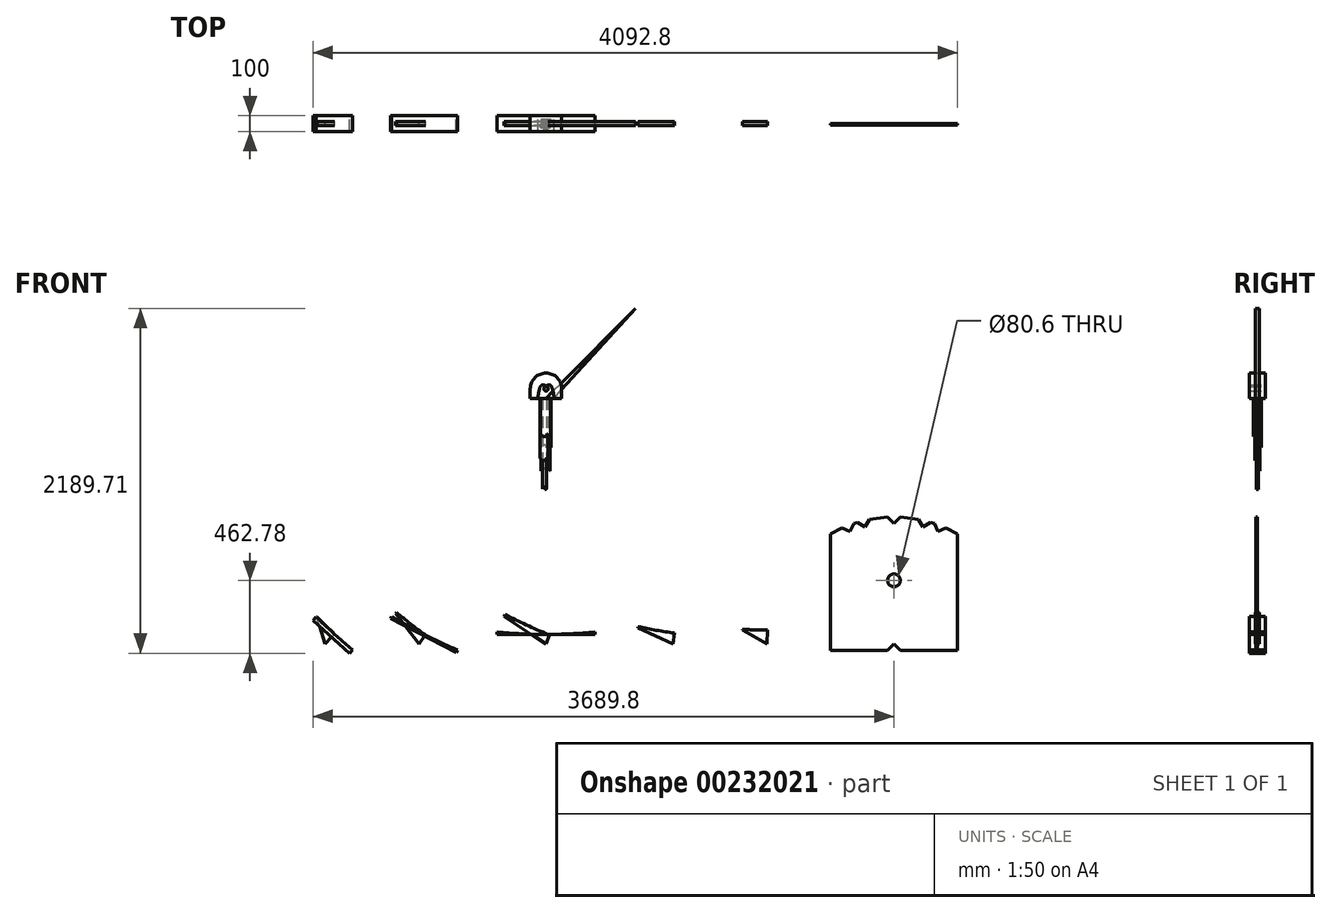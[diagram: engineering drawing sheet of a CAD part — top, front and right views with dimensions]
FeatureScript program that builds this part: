
annotation { "Feature Type Name" : "Feature", "Feature Type Description" : "" }
export const myFeature = defineFeature(function(context is Context, id is Id, definition is map)
    precondition{}
    {
        {
            var Q0;
            Q0=qCreatedBy(makeId("Front.planeOp"),FACE);
            var sketch = newSketch(context, id + "F0", { "sketchPlane" : qUnion([Q0])});
            skCircle(sketch, "E0", {"center": v(0, 0) * mm, "radius": 14 * mm});
            skLineSegment(sketch, "E1", {"start": v(-50, -60) * mm, "end": v(50, -60) * mm, "construction": true});
            skLineSegment(sketch, "E2", {"start": v(0, 0) * mm, "end": v(0, -60) * mm, "construction": true});
            skLineSegment(sketch, "E3", {"start": v(-50, -60) * mm, "end": v(36.5, 12.24) * mm, "construction": true});
            skArc(sketch, "E4", {"start": v(50, -60) * mm, "mid": v(46.6, -23.25) * mm, "end": v(36.5, 12.24) * mm});
            skArc(sketch, "E5", {"start": v(36.5, 12.24) * mm, "mid": v(18.82, 24.99) * mm, "end": v(0, 14) * mm});
            skLineSegment(sketch, "E6", {"start": v(-50, -60) * mm, "end": v(-150, -60) * mm, "construction": true});
            skLineSegment(sketch, "E7.MirrorCS", {"start": v(50, -60) * mm, "end": v(-36.5, 12.24) * mm, "construction": true});
            skArc(sketch, "E8.MirrorCS", {"start": v(-50, -60) * mm, "mid": v(-46.6, -23.25) * mm, "end": v(-36.5, 12.24) * mm});
            skArc(sketch, "E9.MirrorCS", {"start": v(-36.5, 12.24) * mm, "mid": v(-18.82, 24.99) * mm, "end": v(0, 14) * mm});
            skLineSegment(sketch, "E10", {"start": v(0, 120.96) * mm, "end": v(0, -1620) * mm, "construction": true});
            skArc(sketch, "E11", {"start": v(156, -1620) * mm, "mid": v(0, -1464) * mm, "end": v(-156, -1620) * mm, "construction": true});
            skArc(sketch, "E12.1.0.0", {"start": v(-650, -1620) * mm, "mid": v(-806, -1464) * mm, "end": v(-962, -1620) * mm, "construction": true});
            skArc(sketch, "E12.2.0.0", {"start": v(-1248, -1620) * mm, "mid": v(-1404, -1464) * mm, "end": v(-1560, -1620) * mm, "construction": true});
            skLineSegment(sketch, "E13", {"start": v(-806, -1620) * mm, "end": v(0, -1620) * mm, "construction": true});
            skLineSegment(sketch, "E14", {"start": v(-806, -1620) * mm, "end": v(-1404, -1620) * mm, "construction": true});
            skLineSegment(sketch, "E15", {"start": v(-1404, -1620) * mm, "end": v(-2210, -1620) * mm, "construction": true});
            skLineSegment(sketch, "E16", {"start": v(-806, -1620) * mm, "end": v(103.41, 140.15) * mm, "construction": true});
            skLineSegment(sketch, "E17", {"start": v(-1404, -1620) * mm, "end": v(234.43, 200.48) * mm, "construction": true});
            skLineSegment(sketch, "E18.MirrorCS", {"start": v(806, -1620) * mm, "end": v(0, -1620) * mm, "construction": true});
            skArc(sketch, "E19.MirrorCS", {"start": v(650, -1620) * mm, "mid": v(806, -1464) * mm, "end": v(962, -1620) * mm, "construction": true});
            skLineSegment(sketch, "E20.MirrorCS", {"start": v(806, -1620) * mm, "end": v(-103.41, 140.15) * mm, "construction": true});
            skLineSegment(sketch, "E21.MirrorCS", {"start": v(1404, -1620) * mm, "end": v(-234.43, 200.48) * mm, "construction": true});
            skArc(sketch, "E22.MirrorCS", {"start": v(1248, -1620) * mm, "mid": v(1404, -1464) * mm, "end": v(1560, -1620) * mm, "construction": true});
            skLineSegment(sketch, "E23.MirrorCS", {"start": v(1404, -1620) * mm, "end": v(2210, -1620) * mm, "construction": true});
            skLineSegment(sketch, "E24.MirrorCS", {"start": v(806, -1620) * mm, "end": v(1404, -1620) * mm, "construction": true});
            skLineSegment(sketch, "E25", {"start": v(-2210, -1620) * mm, "end": v(-2210, -814) * mm});
            skLineSegment(sketch, "E26", {"start": v(-2210, -1620) * mm, "end": v(-1640.07, -1050.07) * mm, "construction": true});
            skLineSegment(sketch, "E27", {"start": v(-2210, -1620) * mm, "end": v(-1901.56, -875.35) * mm, "construction": true});
            skArc(sketch, "E28", {"start": v(-50, -60) * mm, "mid": v(-47, -77.05) * mm, "end": v(-38.38, -92.05) * mm, "construction": true});
            skLineSegment(sketch, "E29", {"start": v(-38.38, -92.05) * mm, "end": v(0, -60) * mm, "construction": true});
            skArc(sketch, "E30", {"start": v(0, -60) * mm, "mid": v(9.77, -39.12) * mm, "end": v(0, -18.24) * mm, "construction": true});
            skArc(sketch, "E31", {"start": v(-100, 0) * mm, "mid": v(0, 100) * mm, "end": v(100, 0) * mm});
            skLineSegment(sketch, "E32", {"start": v(-100, 0) * mm, "end": v(-100, -60) * mm});
            skLineSegment(sketch, "E33", {"start": v(-100, -60) * mm, "end": v(-50, -60) * mm});
            skLineSegment(sketch, "E34.MirrorCS", {"start": v(100, 0) * mm, "end": v(100, -60) * mm});
            skLineSegment(sketch, "E35.MirrorCS", {"start": v(100, -60) * mm, "end": v(50, -60) * mm});
            skArc(sketch, "E36", {"start": v(-60, -1620) * mm, "mid": v(0, -1560) * mm, "end": v(60, -1620) * mm, "construction": true});
            skArc(sketch, "E37", {"start": v(-874.97, -1620) * mm, "mid": v(-806, -1551.03) * mm, "end": v(-737.03, -1620) * mm, "construction": true});
            skArc(sketch, "E38", {"start": v(-1490.96, -1620) * mm, "mid": v(-1404, -1533.04) * mm, "end": v(-1317.04, -1620) * mm, "construction": true});
            skArc(sketch, "E39.MirrorCS", {"start": v(874.97, -1620) * mm, "mid": v(806, -1551.03) * mm, "end": v(737.03, -1620) * mm, "construction": true});
            skArc(sketch, "E40.MirrorCS", {"start": v(1490.96, -1620) * mm, "mid": v(1404, -1533.04) * mm, "end": v(1317.04, -1620) * mm, "construction": true});
            skArc(sketch, "E41", {"start": v(-1040, -1620) * mm, "mid": v(-806, -1386) * mm, "end": v(-572, -1620) * mm, "construction": true});
            skArc(sketch, "E42", {"start": v(-312, -1620) * mm, "mid": v(0, -1308) * mm, "end": v(312, -1620) * mm, "construction": true});
            skLineSegment(sketch, "E43", {"start": v(-958.6, -1442.61) * mm, "end": v(-1302.26, -1738.26) * mm, "construction": true});
            skLineSegment(sketch, "E44", {"start": v(-211.35, -1390.5) * mm, "end": v(-647.48, -1792.13) * mm, "construction": true});
            skSolve(sketch);
        }
        {
            var Q0;
            Q0=qCreatedBy(makeId("Front.planeOp"),FACE);
            var sketch = newSketch(context, id + "F1", { "sketchPlane" : qUnion([Q0])});
            skPoint(sketch, "E45.0", {"position": v(-1404, -1620) * mm});
            skPoint(sketch, "E46.0", {"position": v(-806, -1620) * mm});
            skPoint(sketch, "E47.0", {"position": v(0, -1620) * mm});
            skPoint(sketch, "E48.0", {"position": v(806, -1620) * mm});
            skPoint(sketch, "E49.0", {"position": v(1404, -1620) * mm});
            skLineSegment(sketch, "E50.0", {"start": v(-1404, -1620) * mm, "end": v(234.43, 200.48) * mm, "construction": true});
            skLineSegment(sketch, "E51.0", {"start": v(-806, -1620) * mm, "end": v(103.41, 140.15) * mm, "construction": true});
            skLineSegment(sketch, "E52.0", {"start": v(0, 120.96) * mm, "end": v(0, -1620) * mm, "construction": true});
            skLineSegment(sketch, "E53.0", {"start": v(806, -1620) * mm, "end": v(-103.41, 140.15) * mm, "construction": true});
            skLineSegment(sketch, "E54.0", {"start": v(1404, -1620) * mm, "end": v(-234.43, 200.48) * mm, "construction": true});
            skLineSegment(sketch, "E55.0", {"start": v(-2210, -1620) * mm, "end": v(-2210, -814) * mm, "construction": true});
            skPoint(sketch, "E56.0", {"position": v(2210, -1620) * mm});
            skArc(sketch, "E57", {"start": v(-1317.04, -1620) * mm, "mid": v(-1404, -1533.04) * mm, "end": v(-1490.96, -1620) * mm, "construction": true});
            skArc(sketch, "E58.1.0.0", {"start": v(-737.03, -1620) * mm, "mid": v(-806, -1551.03) * mm, "end": v(-874.97, -1620) * mm, "construction": true});
            skArc(sketch, "E58.2.0.0", {"start": v(60, -1620) * mm, "mid": v(0, -1560) * mm, "end": v(-60, -1620) * mm, "construction": true});
            skArc(sketch, "E58.3.0.0", {"start": v(874.97, -1620) * mm, "mid": v(806, -1551.03) * mm, "end": v(737.03, -1620) * mm, "construction": true});
            skArc(sketch, "E58.4.0.0", {"start": v(1490.96, -1620) * mm, "mid": v(1404, -1533.04) * mm, "end": v(1317.04, -1620) * mm, "construction": true});
            skLineSegment(sketch, "E59", {"start": v(0, -1620) * mm, "end": v(0, -1560) * mm, "construction": true});
            skLineSegment(sketch, "E60", {"start": v(789.43, -1553.05) * mm, "end": v(806, -1620) * mm, "construction": true});
            skLineSegment(sketch, "E61", {"start": v(1372.32, -1539.02) * mm, "end": v(1404, -1620) * mm, "construction": true});
            skLineSegment(sketch, "E62", {"start": v(-1372.32, -1539.02) * mm, "end": v(-1404, -1620) * mm, "construction": true});
            skLineSegment(sketch, "E63", {"start": v(-789.43, -1553.05) * mm, "end": v(-806, -1620) * mm, "construction": true});
            skLineSegment(sketch, "E64", {"start": v(2210, -1620) * mm, "end": v(2503.62, -869.39) * mm, "construction": true});
            skLineSegment(sketch, "E65", {"start": v(2016.36, -837.6) * mm, "end": v(2210, -1620) * mm, "construction": true});
            skLineSegment(sketch, "E66", {"start": v(2210, -814) * mm, "end": v(2210, -1620) * mm, "construction": true});
            skLineSegment(sketch, "E67", {"start": v(2403.64, -837.6) * mm, "end": v(2210, -1620) * mm, "construction": true});
            skLineSegment(sketch, "E68", {"start": v(1916.38, -869.39) * mm, "end": v(2210, -1620) * mm, "construction": true});
            skLineSegment(sketch, "E69", {"start": v(-1372.32, -1539.02) * mm, "end": v(-825.43, -946.95) * mm, "construction": true});
            skLineSegment(sketch, "E70", {"start": v(-789.43, -1553.05) * mm, "end": v(-413.48, -840.1) * mm, "construction": true});
            skLineSegment(sketch, "E71", {"start": v(0, -1560) * mm, "end": v(0, -754) * mm, "construction": true});
            skLineSegment(sketch, "E72", {"start": v(789.43, -1553.05) * mm, "end": v(413.48, -840.1) * mm, "construction": true});
            skLineSegment(sketch, "E73", {"start": v(1372.32, -1539.02) * mm, "end": v(825.43, -946.95) * mm, "construction": true});
            skLineSegment(sketch, "E74", {"start": v(-1372.32, -1539.02) * mm, "end": v(-1372.32, -733.02) * mm, "construction": true});
            skLineSegment(sketch, "E75", {"start": v(-789.43, -1553.05) * mm, "end": v(-789.43, -747.05) * mm, "construction": true});
            skLineSegment(sketch, "E76", {"start": v(789.43, -1553.05) * mm, "end": v(789.43, -747.05) * mm, "construction": true});
            skLineSegment(sketch, "E77", {"start": v(1372.32, -1539.02) * mm, "end": v(1372.32, -733.02) * mm, "construction": true});
            skCircle(sketch, "E78", {"center": v(2210, -1620) * mm, "radius": 806 * mm, "construction": true});
            skCircle(sketch, "E79", {"center": v(1916.38, -869.39) * mm, "radius": 40.3 * mm, "construction": true});
            skCircle(sketch, "E80", {"center": v(2210, -814) * mm, "radius": 40.3 * mm, "construction": true});
            skCircle(sketch, "E81", {"center": v(2016.36, -837.6) * mm, "radius": 40.3 * mm, "construction": true});
            skCircle(sketch, "E82", {"center": v(2403.64, -837.6) * mm, "radius": 40.3 * mm, "construction": true});
            skCircle(sketch, "E83", {"center": v(2503.62, -869.39) * mm, "radius": 40.3 * mm, "construction": true});
            skLineSegment(sketch, "E84", {"start": v(1879.23, -885) * mm, "end": v(1931.06, -906.92) * mm});
            skLineSegment(sketch, "E85", {"start": v(1931.06, -906.92) * mm, "end": v(1954.27, -855.65) * mm});
            skLineSegment(sketch, "E86", {"start": v(1954.27, -855.65) * mm, "end": v(1977.49, -848.26) * mm});
            skLineSegment(sketch, "E87", {"start": v(1977.49, -848.26) * mm, "end": v(2026.04, -876.73) * mm});
            skLineSegment(sketch, "E88", {"start": v(2026.04, -876.73) * mm, "end": v(2055.7, -828.9) * mm});
            skLineSegment(sketch, "E89", {"start": v(2169.71, -815) * mm, "end": v(2210, -854.3) * mm});
            skLineSegment(sketch, "E90", {"start": v(2210, -854.3) * mm, "end": v(2250.29, -815) * mm});
            skLineSegment(sketch, "E91", {"start": v(2250.29, -815) * mm, "end": v(2364.3, -828.9) * mm});
            skLineSegment(sketch, "E92", {"start": v(2364.3, -828.9) * mm, "end": v(2393.96, -876.73) * mm});
            skLineSegment(sketch, "E93", {"start": v(2393.96, -876.73) * mm, "end": v(2442.51, -848.26) * mm});
            skLineSegment(sketch, "E94", {"start": v(2442.51, -848.26) * mm, "end": v(2465.73, -855.65) * mm});
            skLineSegment(sketch, "E95", {"start": v(2465.73, -855.65) * mm, "end": v(2488.94, -906.92) * mm});
            skLineSegment(sketch, "E96", {"start": v(2488.94, -906.92) * mm, "end": v(2540.77, -885) * mm});
            skLineSegment(sketch, "E97", {"start": v(2055.7, -828.9) * mm, "end": v(2169.71, -815) * mm});
            skLineSegment(sketch, "E98", {"start": v(1807, -1660.3) * mm, "end": v(2169.7, -1660.3) * mm});
            skLineSegment(sketch, "E99", {"start": v(2210, -1620) * mm, "end": v(2210, -1660.3) * mm, "construction": true});
            skArc(sketch, "E100", {"start": v(2250.3, -1660.3) * mm, "mid": v(2210, -1620) * mm, "end": v(2169.7, -1660.3) * mm, "construction": true});
            skLineSegment(sketch, "E101", {"start": v(2210, -1620) * mm, "end": v(3016, -1620) * mm, "construction": true});
            skLineSegment(sketch, "E102", {"start": v(2613, -1660.3) * mm, "end": v(2613, -921.98) * mm});
            skPoint(sketch, "E103", {"position": v(2613, -1620) * mm});
            skLineSegment(sketch, "E104.MirrorCS", {"start": v(1807, -1660.3) * mm, "end": v(1807, -921.98) * mm});
            skLineSegment(sketch, "E105", {"start": v(1879.23, -885) * mm, "end": v(1807, -921.98) * mm});
            skLineSegment(sketch, "E106", {"start": v(2169.7, -1660.3) * mm, "end": v(2210, -1620) * mm});
            skLineSegment(sketch, "E107", {"start": v(2210, -1620) * mm, "end": v(2250.3, -1660.3) * mm});
            skLineSegment(sketch, "E108.trimOffspring", {"start": v(2250.3, -1660.3) * mm, "end": v(2613, -1660.3) * mm});
            skLineSegment(sketch, "E109", {"start": v(2540.77, -885) * mm, "end": v(2613, -921.98) * mm});
            skLineSegment(sketch, "E110", {"start": v(2210, -1620) * mm, "end": v(2210, -814) * mm, "construction": true});
            skCircle(sketch, "E111", {"center": v(2210, -1217) * mm, "radius": 40.3 * mm});
            skSolve(sketch);
        }
        {
            var Q0;
            Q0=qCreatedBy(makeId("Front.planeOp"),FACE);
            var sketch = newSketch(context, id + "F2", { "sketchPlane" : qUnion([Q0])});
            skArc(sketch, "E112.2", {"start": v(60, -1620) * mm, "mid": v(0, -1560) * mm, "end": v(-60, -1620) * mm, "construction": true});
            skLineSegment(sketch, "E113.2", {"start": v(0, 120.96) * mm, "end": v(0, -1620) * mm, "construction": true});
            skLineSegment(sketch, "E114", {"start": v(0, -1620) * mm, "end": v(0, -1560) * mm, "construction": true});
            skLineSegment(sketch, "E115", {"start": v(-312, -1560) * mm, "end": v(312, -1560) * mm, "construction": true});
            skLineSegment(sketch, "E116", {"start": v(-312, -1560) * mm, "end": v(-312, -1545.55) * mm, "construction": true});
            skLineSegment(sketch, "E117", {"start": v(-312, -1545.55) * mm, "end": v(0, 120.96) * mm, "construction": true});
            skLineSegment(sketch, "E118", {"start": v(0, 120.96) * mm, "end": v(312, -1545.55) * mm, "construction": true});
            skLineSegment(sketch, "E119", {"start": v(312, -1545.55) * mm, "end": v(312, -1560) * mm, "construction": true});
            skLineSegment(sketch, "E120", {"start": v(0, -936) * mm, "end": v(0, -1560) * mm, "construction": true});
            skLineSegment(sketch, "E121", {"start": v(0, 120.96) * mm, "end": v(0, -1560) * mm, "construction": true});
            skLineSegment(sketch, "E122", {"start": v(312, -1545.55) * mm, "end": v(312, -921.55) * mm, "construction": true});
            skLineSegment(sketch, "E123", {"start": v(312, -1545.55) * mm, "end": v(0, 1816.43) * mm, "construction": true});
            skArc(sketch, "E124", {"start": v(0, -1560) * mm, "mid": v(-156.17, -1556.39) * mm, "end": v(-312, -1545.55) * mm});
            skLineSegment(sketch, "E125", {"start": v(-312, -1545.55) * mm, "end": v(-312, -921.55) * mm, "construction": true});
            skLineSegment(sketch, "E126", {"start": v(-312, -1545.55) * mm, "end": v(0, 1816.43) * mm, "construction": true});
            skArc(sketch, "E127", {"start": v(0, -1560) * mm, "mid": v(156.17, -1556.39) * mm, "end": v(312, -1545.55) * mm});
            skLineSegment(sketch, "E128", {"start": v(-312, -1545.55) * mm, "end": v(-312, -1560) * mm});
            skLineSegment(sketch, "E129", {"start": v(-312, -1560) * mm, "end": v(312, -1560) * mm});
            skLineSegment(sketch, "E130", {"start": v(312, -1560) * mm, "end": v(312, -1545.55) * mm});
            skLineSegment(sketch, "E131", {"start": v(312, -1545.55) * mm, "end": v(936, -1545.55) * mm, "construction": true});
            skSolve(sketch);
        }
        {
            var Q0;
            Q0=qCreatedBy(makeId("Front.planeOp"),FACE);
            var sketch = newSketch(context, id + "F3", { "sketchPlane" : qUnion([Q0])});
            skArc(sketch, "E132.0", {"start": v(-737.03, -1620) * mm, "mid": v(-806, -1551.03) * mm, "end": v(-874.97, -1620) * mm, "construction": true});
            skLineSegment(sketch, "E133.0", {"start": v(-806, -1620) * mm, "end": v(103.41, 140.15) * mm, "construction": true});
            skLineSegment(sketch, "E134", {"start": v(-806, -1620) * mm, "end": v(-774.51, -1558.64) * mm, "construction": true});
            skLineSegment(sketch, "E135", {"start": v(-982.7, -1451.8) * mm, "end": v(-566.32, -1665.47) * mm, "construction": true});
            skLineSegment(sketch, "E136", {"start": v(-562.05, -1141.65) * mm, "end": v(-774.51, -1558.64) * mm, "construction": true});
            skLineSegment(sketch, "E137", {"start": v(-774.51, -1558.64) * mm, "end": v(103.41, 140.15) * mm, "construction": true});
            skLineSegment(sketch, "E138", {"start": v(-982.7, -1451.8) * mm, "end": v(-979.44, -1445.45) * mm, "construction": true});
            skLineSegment(sketch, "E139", {"start": v(-979.44, -1445.45) * mm, "end": v(103.41, 140.15) * mm, "construction": true});
            skLineSegment(sketch, "E140", {"start": v(-566.32, -1665.47) * mm, "end": v(-563.06, -1659.1) * mm, "construction": true});
            skLineSegment(sketch, "E141", {"start": v(-563.06, -1659.1) * mm, "end": v(103.41, 140.15) * mm, "construction": true});
            skLineSegment(sketch, "E142", {"start": v(-563.06, -1659.1) * mm, "end": v(974.37, 1849.47) * mm, "construction": true});
            skArc(sketch, "E143", {"start": v(-774.51, -1558.64) * mm, "mid": v(-669.55, -1610.5) * mm, "end": v(-563.06, -1659.1) * mm});
            skLineSegment(sketch, "E144", {"start": v(-563.06, -1659.1) * mm, "end": v(-350.6, -1242.12) * mm, "construction": true});
            skArc(sketch, "E145", {"start": v(-774.51, -1558.64) * mm, "mid": v(-877.84, -1503.6) * mm, "end": v(-979.44, -1445.45) * mm});
            skLineSegment(sketch, "E146", {"start": v(975.3, 1851.26) * mm, "end": v(-979.44, -1445.45) * mm, "construction": true});
            skLineSegment(sketch, "E147", {"start": v(-979.44, -1445.45) * mm, "end": v(-766.97, -1028.46) * mm, "construction": true});
            skLineSegment(sketch, "E148", {"start": v(-979.44, -1445.45) * mm, "end": v(-986.8, -1459.79) * mm});
            skLineSegment(sketch, "E149", {"start": v(-986.8, -1459.79) * mm, "end": v(-570.42, -1673.45) * mm});
            skLineSegment(sketch, "E150", {"start": v(-570.42, -1673.45) * mm, "end": v(-563.06, -1659.1) * mm});
            skLineSegment(sketch, "E151", {"start": v(-563.06, -1659.1) * mm, "end": v(-95.06, -1659.1) * mm, "construction": true});
            skSolve(sketch);
        }
        {
            var Q0;
            Q0=qCreatedBy(makeId("Front.planeOp"),FACE);
            var sketch = newSketch(context, id + "F4", { "sketchPlane" : qUnion([Q0])});
            skLineSegment(sketch, "E152.0", {"start": v(-1404, -1620) * mm, "end": v(234.43, 200.48) * mm, "construction": true});
            skArc(sketch, "E153.0", {"start": v(-1317.04, -1620) * mm, "mid": v(-1404, -1533.04) * mm, "end": v(-1490.96, -1620) * mm, "construction": true});
            skLineSegment(sketch, "E154", {"start": v(-1404, -1620) * mm, "end": v(-1345.82, -1555.37) * mm, "construction": true});
            skLineSegment(sketch, "E155", {"start": v(-1345.82, -1555.37) * mm, "end": v(234.43, 200.48) * mm, "construction": true});
            skLineSegment(sketch, "E156", {"start": v(-1345.82, -1555.37) * mm, "end": v(-1137.05, -1323.51) * mm, "construction": true});
            skLineSegment(sketch, "E157", {"start": v(-1461.76, -1451) * mm, "end": v(-1229.88, -1659.74) * mm, "construction": true});
            skLineSegment(sketch, "E158", {"start": v(-1229.88, -1659.74) * mm, "end": v(-1228.16, -1657.83) * mm, "construction": true});
            skLineSegment(sketch, "E159", {"start": v(-1228.16, -1657.83) * mm, "end": v(234.43, 200.48) * mm, "construction": true});
            skLineSegment(sketch, "E160", {"start": v(-1461.76, -1451) * mm, "end": v(-1460.04, -1449.09) * mm, "construction": true});
            skLineSegment(sketch, "E161", {"start": v(-1460.04, -1449.09) * mm, "end": v(234.43, 200.48) * mm, "construction": true});
            skArc(sketch, "E162", {"start": v(-1345.82, -1555.37) * mm, "mid": v(-1287.41, -1607.09) * mm, "end": v(-1228.16, -1657.83) * mm});
            skLineSegment(sketch, "E163", {"start": v(-1228.16, -1657.83) * mm, "end": v(-1019.39, -1425.97) * mm, "construction": true});
            skLineSegment(sketch, "E164", {"start": v(-1228.16, -1657.83) * mm, "end": v(1816.82, 1957.9) * mm, "construction": true});
            skArc(sketch, "E165", {"start": v(-1345.82, -1555.37) * mm, "mid": v(-1403.37, -1502.7) * mm, "end": v(-1460.04, -1449.09) * mm});
            skLineSegment(sketch, "E166", {"start": v(-1251.27, -1217.23) * mm, "end": v(-1460.04, -1449.09) * mm, "construction": true});
            skLineSegment(sketch, "E167", {"start": v(-1460.04, -1449.09) * mm, "end": v(1816.78, 1957.86) * mm, "construction": true});
            skLineSegment(sketch, "E168", {"start": v(-1460.04, -1449.09) * mm, "end": v(-1479.8, -1471.04) * mm});
            skLineSegment(sketch, "E169", {"start": v(-1479.8, -1471.04) * mm, "end": v(-1247.91, -1679.78) * mm});
            skLineSegment(sketch, "E170", {"start": v(-1247.91, -1679.78) * mm, "end": v(-1228.16, -1657.83) * mm});
            skLineSegment(sketch, "E171", {"start": v(-1228.16, -1657.83) * mm, "end": v(-916.16, -1657.83) * mm, "construction": true});
            skSolve(sketch);
        }
        {
            var Q0;
            Q0=qCreatedBy(makeId("Front.planeOp"),FACE);
            var sketch = newSketch(context, id + "F5", { "sketchPlane" : qUnion([Q0])});
            skLineSegment(sketch, "E172.0", {"start": v(-1372.32, -1539.02) * mm, "end": v(-1404, -1620) * mm, "construction": true});
            skLineSegment(sketch, "E173.0", {"start": v(-789.43, -1553.05) * mm, "end": v(-806, -1620) * mm, "construction": true});
            skLineSegment(sketch, "E174.0", {"start": v(789.43, -1553.05) * mm, "end": v(806, -1620) * mm, "construction": true});
            skLineSegment(sketch, "E175.0", {"start": v(0, -1620) * mm, "end": v(0, -1560) * mm, "construction": true});
            skLineSegment(sketch, "E176.0", {"start": v(1372.32, -1539.02) * mm, "end": v(1404, -1620) * mm, "construction": true});
            skLineSegment(sketch, "E177", {"start": v(-1404, -1620) * mm, "end": v(-1690.2, -1508.05) * mm, "construction": true});
            skLineSegment(sketch, "E178", {"start": v(-1690.2, -1508.05) * mm, "end": v(-679.1, -855.58) * mm, "construction": true});
            skLineSegment(sketch, "E179", {"start": v(-679.1, -855.58) * mm, "end": v(-1404, -1620) * mm, "construction": true});
            skLineSegment(sketch, "E180", {"start": v(-806, -1620) * mm, "end": v(-1104.32, -1546.17) * mm, "construction": true});
            skLineSegment(sketch, "E181", {"start": v(-1104.32, -1546.17) * mm, "end": v(-186.52, -767.9) * mm, "construction": true});
            skLineSegment(sketch, "E182", {"start": v(-186.52, -767.9) * mm, "end": v(-806, -1620) * mm, "construction": true});
            skLineSegment(sketch, "E183", {"start": v(-307.32, -1620) * mm, "end": v(396.62, -644.04) * mm, "construction": true});
            skLineSegment(sketch, "E184", {"start": v(396.62, -644.04) * mm, "end": v(0, -1620) * mm, "construction": true});
            skLineSegment(sketch, "E185", {"start": v(806, -1620) * mm, "end": v(507.68, -1693.83) * mm, "construction": true});
            skLineSegment(sketch, "E186", {"start": v(507.68, -1693.83) * mm, "end": v(956.52, -577.33) * mm, "construction": true});
            skLineSegment(sketch, "E187", {"start": v(956.52, -577.33) * mm, "end": v(806, -1620) * mm, "construction": true});
            skLineSegment(sketch, "E188", {"start": v(1404, -1620) * mm, "end": v(1117.8, -1731.95) * mm, "construction": true});
            skLineSegment(sketch, "E189", {"start": v(1117.8, -1731.95) * mm, "end": v(1417.82, -566.61) * mm, "construction": true});
            skLineSegment(sketch, "E190", {"start": v(1417.82, -566.61) * mm, "end": v(1404, -1620) * mm, "construction": true});
            skLineSegment(sketch, "E191.0", {"start": v(0, 120.96) * mm, "end": v(0, -1620) * mm, "construction": true});
            skLineSegment(sketch, "E192.0", {"start": v(-2210, -1620) * mm, "end": v(-1640.07, -1050.07) * mm, "construction": true});
            skArc(sketch, "E193", {"start": v(-1372.32, -1539.02) * mm, "mid": v(-1450.62, -1693.4) * mm, "end": v(-1344.16, -1556.9) * mm});
            skArc(sketch, "E194", {"start": v(-789.43, -1553.05) * mm, "mid": v(-835.1, -1682.52) * mm, "end": v(-765.45, -1564.22) * mm});
            skArc(sketch, "E195", {"start": v(0, -1560) * mm, "mid": v(-11.5, -1678.89) * mm, "end": v(22.59, -1564.41) * mm});
            skArc(sketch, "E196", {"start": v(789.43, -1553.05) * mm, "mid": v(809.42, -1688.88) * mm, "end": v(815.85, -1551.74) * mm});
            skArc(sketch, "E197", {"start": v(1372.32, -1539.02) * mm, "mid": v(1419.56, -1705.55) * mm, "end": v(1405.14, -1533.05) * mm});
            skLineSegment(sketch, "E198", {"start": v(-1457.36, -1449.56) * mm, "end": v(-1230.97, -1664.25) * mm});
            skLineSegment(sketch, "E199", {"start": v(-954.71, -1426.62) * mm, "end": v(-576.18, -1701.82) * mm});
            skLineSegment(sketch, "E200", {"start": v(-266.45, -1446.95) * mm, "end": v(311.63, -1681.88) * mm});
            skLineSegment(sketch, "E201", {"start": v(584.25, -1518.3) * mm, "end": v(1047.45, -1585.18) * mm});
            skLineSegment(sketch, "E202", {"start": v(1249.15, -1531) * mm, "end": v(1561.13, -1535.1) * mm});
            skLineSegment(sketch, "E203", {"start": v(0, 120.96) * mm, "end": v(22.59, -1564.41) * mm, "construction": true});
            skLineSegment(sketch, "E204", {"start": v(22.59, -1564.41) * mm, "end": v(592.52, -994.49) * mm, "construction": true});
            skLineSegment(sketch, "E205", {"start": v(0, -1620) * mm, "end": v(-307.32, -1620) * mm, "construction": true});
            skSolve(sketch);
        }
        {
            var Q0;
            Q0=qCreatedBy(makeId("Front.planeOp"),FACE);
            var sketch = newSketch(context, id + "F6", { "sketchPlane" : qUnion([Q0])});
            skLineSegment(sketch, "E206.0", {"start": v(-266.45, -1446.95) * mm, "end": v(311.63, -1681.88) * mm});
            skLineSegment(sketch, "E207.0", {"start": v(-50, -60) * mm, "end": v(50, -60) * mm, "construction": true});
            skArc(sketch, "E207.1", {"start": v(-50, -60) * mm, "mid": v(-46.6, -23.25) * mm, "end": v(-36.5, 12.24) * mm, "construction": true});
            skArc(sketch, "E207.2", {"start": v(-36.5, 12.24) * mm, "mid": v(-18.82, 24.99) * mm, "end": v(0, 14) * mm, "construction": true});
            skArc(sketch, "E207.3", {"start": v(36.5, 12.24) * mm, "mid": v(18.82, 24.99) * mm, "end": v(0, 14) * mm, "construction": true});
            skArc(sketch, "E207.4", {"start": v(50, -60) * mm, "mid": v(46.6, -23.25) * mm, "end": v(36.5, 12.24) * mm, "construction": true});
            skCircle(sketch, "E207.5", {"center": v(0, 0) * mm, "radius": 14 * mm, "construction": true});
            skLineSegment(sketch, "E208.0", {"start": v(-2210, -1620) * mm, "end": v(-1640.07, -1050.07) * mm, "construction": true});
            skLineSegment(sketch, "E209.0", {"start": v(-312, -1545.55) * mm, "end": v(0, 1816.43) * mm, "construction": true});
            skLineSegment(sketch, "E210.0", {"start": v(312, -1545.55) * mm, "end": v(0, 1816.43) * mm, "construction": true});
            skLineSegment(sketch, "E211", {"start": v(22.59, -1564.41) * mm, "end": v(1293.76, 1563.59) * mm, "construction": true});
            skLineSegment(sketch, "E212", {"start": v(1293.76, 1563.59) * mm, "end": v(-261.02, -1433.57) * mm, "construction": true});
            skLineSegment(sketch, "E213", {"start": v(-261.02, -1433.57) * mm, "end": v(-266.45, -1446.95) * mm, "construction": true});
            skLineSegment(sketch, "E214", {"start": v(-261.02, -1433.57) * mm, "end": v(308.91, -863.64) * mm, "construction": true});
            skLineSegment(sketch, "E215", {"start": v(-261.02, -1433.57) * mm, "end": v(-22.87, -60) * mm, "construction": true});
            skLineSegment(sketch, "E216", {"start": v(1293.76, 1563.59) * mm, "end": v(317.07, -1668.5) * mm, "construction": true});
            skLineSegment(sketch, "E217", {"start": v(317.07, -1668.5) * mm, "end": v(311.63, -1681.88) * mm, "construction": true});
            skLineSegment(sketch, "E218", {"start": v(317.07, -1668.5) * mm, "end": v(887, -1098.57) * mm, "construction": true});
            skLineSegment(sketch, "E219", {"start": v(317.07, -1668.5) * mm, "end": v(-6.44, -60) * mm, "construction": true});
            skLineSegment(sketch, "E220", {"start": v(887, -1098.57) * mm, "end": v(480.5, -692.06) * mm, "construction": true});
            skLineSegment(sketch, "E221", {"start": v(-547.34, -2134.34) * mm, "end": v(22.59, -1564.41) * mm, "construction": true});
            skLineSegment(sketch, "E222", {"start": v(2.43, -60) * mm, "end": v(22.59, -1564.41) * mm, "construction": true});
            skArc(sketch, "E223.0", {"start": v(60, -1620) * mm, "mid": v(0, -1560) * mm, "end": v(-60, -1620) * mm, "construction": true});
            skLineSegment(sketch, "E224.bottom", {"start": v(-22.87, -60) * mm, "end": v(2.43, -60) * mm});
            skLineSegment(sketch, "E224.top", {"start": v(-22.87, -634.89) * mm, "end": v(2.43, -634.89) * mm, "construction": true});
            skLineSegment(sketch, "E224.left", {"start": v(2.43, -60) * mm, "end": v(2.43, -634.89) * mm});
            skLineSegment(sketch, "E224.right", {"start": v(-22.87, -60) * mm, "end": v(-22.87, -634.89) * mm});
            skLineSegment(sketch, "E225.bottom", {"start": v(-6.44, -60) * mm, "end": v(2.43, -60) * mm});
            skLineSegment(sketch, "E225.top", {"start": v(-6.44, -634.89) * mm, "end": v(2.43, -634.89) * mm, "construction": true});
            skLineSegment(sketch, "E225.right", {"start": v(-6.44, -60) * mm, "end": v(-6.44, -634.89) * mm});
            skArc(sketch, "E226", {"start": v(2.43, -634.89) * mm, "mid": v(-2, -639.32) * mm, "end": v(-6.44, -634.89) * mm});
            skArc(sketch, "E227", {"start": v(-22.87, -634.89) * mm, "mid": v(-10.22, -622.24) * mm, "end": v(2.43, -634.89) * mm});
            skSolve(sketch);
        }
        {
            var Q0;
            Q0=qCreatedBy(makeId("Front.planeOp"),FACE);
            var sketch = newSketch(context, id + "F7", { "sketchPlane" : qUnion([Q0])});
            skLineSegment(sketch, "E228.0", {"start": v(-50, -60) * mm, "end": v(50, -60) * mm, "construction": true});
            skArc(sketch, "E229.0", {"start": v(-50, -60) * mm, "mid": v(-46.6, -23.25) * mm, "end": v(-36.5, 12.24) * mm, "construction": true});
            skArc(sketch, "E229.1", {"start": v(-36.5, 12.24) * mm, "mid": v(-18.82, 24.99) * mm, "end": v(0, 14) * mm, "construction": true});
            skCircle(sketch, "E229.2", {"center": v(0, 0) * mm, "radius": 14 * mm, "construction": true});
            skArc(sketch, "E229.3", {"start": v(36.5, 12.24) * mm, "mid": v(18.82, 24.99) * mm, "end": v(0, 14) * mm, "construction": true});
            skArc(sketch, "E229.4", {"start": v(50, -60) * mm, "mid": v(46.6, -23.25) * mm, "end": v(36.5, 12.24) * mm, "construction": true});
            skLineSegment(sketch, "E230.0", {"start": v(-954.71, -1426.62) * mm, "end": v(-576.18, -1701.82) * mm});
            skLineSegment(sketch, "E231.0", {"start": v(584.25, -1518.3) * mm, "end": v(1047.45, -1585.18) * mm});
            skPoint(sketch, "E232.0", {"position": v(-765.45, -1564.22) * mm});
            skPoint(sketch, "E233.0", {"position": v(815.85, -1551.74) * mm});
            skLineSegment(sketch, "E234.0", {"start": v(975.3, 1851.26) * mm, "end": v(-979.44, -1445.45) * mm, "construction": true});
            skLineSegment(sketch, "E234.1", {"start": v(-563.06, -1659.1) * mm, "end": v(974.37, 1849.47) * mm, "construction": true});
            skLineSegment(sketch, "E235", {"start": v(815.85, -1551.74) * mm, "end": v(1363.17, 2239.6) * mm, "construction": true});
            skLineSegment(sketch, "E236", {"start": v(1363.17, 2239.6) * mm, "end": v(585.28, -1511.23) * mm, "construction": true});
            skLineSegment(sketch, "E237", {"start": v(585.28, -1511.23) * mm, "end": v(584.25, -1518.3) * mm, "construction": true});
            skLineSegment(sketch, "E238", {"start": v(585.28, -1511.23) * mm, "end": v(1155.2, -941.3) * mm, "construction": true});
            skLineSegment(sketch, "E239", {"start": v(585.28, -1511.23) * mm, "end": v(11.67, -60) * mm, "construction": true});
            skLineSegment(sketch, "E240.0", {"start": v(-2210, -1620) * mm, "end": v(-1640.07, -1050.07) * mm, "construction": true});
            skLineSegment(sketch, "E241", {"start": v(478.55, -2148.03) * mm, "end": v(1048.47, -1578.1) * mm, "construction": true});
            skLineSegment(sketch, "E242", {"start": v(-37.24, -60) * mm, "end": v(1048.47, -1578.1) * mm, "construction": true});
            skLineSegment(sketch, "E243", {"start": v(1047.45, -1585.18) * mm, "end": v(1048.47, -1578.1) * mm, "construction": true});
            skLineSegment(sketch, "E244", {"start": v(815.85, -1551.74) * mm, "end": v(1363.46, 2241.6) * mm, "construction": true});
            skLineSegment(sketch, "E245", {"start": v(1363.46, 2241.6) * mm, "end": v(1048.47, -1578.1) * mm, "construction": true});
            skLineSegment(sketch, "E246", {"start": v(478.55, -2148.03) * mm, "end": v(213.51, -1883) * mm, "construction": true});
            skLineSegment(sketch, "E247", {"start": v(-1520.44, -1990.76) * mm, "end": v(-950.5, -1420.84) * mm, "construction": true});
            skLineSegment(sketch, "E248", {"start": v(-31.38, -60) * mm, "end": v(-950.5, -1420.84) * mm, "construction": true});
            skLineSegment(sketch, "E249", {"start": v(-765.45, -1564.22) * mm, "end": v(1488.29, 1535.78) * mm, "construction": true});
            skLineSegment(sketch, "E250", {"start": v(1488.29, 1535.78) * mm, "end": v(-950.5, -1420.84) * mm, "construction": true});
            skLineSegment(sketch, "E251", {"start": v(-950.5, -1420.84) * mm, "end": v(-954.71, -1426.62) * mm, "construction": true});
            skLineSegment(sketch, "E252", {"start": v(-576.18, -1701.82) * mm, "end": v(-571.97, -1696.03) * mm, "construction": true});
            skLineSegment(sketch, "E253", {"start": v(-765.45, -1564.22) * mm, "end": v(1487.1, 1534.14) * mm, "construction": true});
            skLineSegment(sketch, "E254", {"start": v(1487.1, 1534.14) * mm, "end": v(-571.97, -1696.03) * mm, "construction": true});
            skLineSegment(sketch, "E255", {"start": v(-1468.77, -1939.1) * mm, "end": v(-1141.9, -2265.96) * mm, "construction": true});
            skLineSegment(sketch, "E256", {"start": v(-571.97, -1696.03) * mm, "end": v(-1141.9, -2265.96) * mm, "construction": true});
            skLineSegment(sketch, "E257", {"start": v(24.5, -60) * mm, "end": v(-571.97, -1696.03) * mm, "construction": true});
            skLineSegment(sketch, "E258", {"start": v(1385.78, -981.81) * mm, "end": v(815.85, -1551.74) * mm, "construction": true});
            skLineSegment(sketch, "E259", {"start": v(815.85, -1551.74) * mm, "end": v(3.51, -60) * mm, "construction": true});
            skLineSegment(sketch, "E260", {"start": v(-1335.37, -2134.15) * mm, "end": v(-765.45, -1564.22) * mm, "construction": true});
            skLineSegment(sketch, "E261", {"start": v(2.16, -60) * mm, "end": v(-765.45, -1564.22) * mm, "construction": true});
            skArc(sketch, "E262.0", {"start": v(-737.03, -1620) * mm, "mid": v(-806, -1551.03) * mm, "end": v(-874.97, -1620) * mm, "construction": true});
            skArc(sketch, "E263.0", {"start": v(874.97, -1620) * mm, "mid": v(806, -1551.03) * mm, "end": v(737.03, -1620) * mm, "construction": true});
            skLineSegment(sketch, "E264.bottom", {"start": v(3.51, -60) * mm, "end": v(11.67, -60) * mm});
            skLineSegment(sketch, "E264.top", {"start": v(3.51, -434.82) * mm, "end": v(11.67, -434.82) * mm, "construction": true});
            skLineSegment(sketch, "E264.left", {"start": v(11.67, -60) * mm, "end": v(11.67, -434.82) * mm});
            skLineSegment(sketch, "E264.right", {"start": v(3.51, -60) * mm, "end": v(3.51, -434.82) * mm});
            skArc(sketch, "E265", {"start": v(11.67, -434.82) * mm, "mid": v(7.6, -438.9) * mm, "end": v(3.51, -434.82) * mm});
            skLineSegment(sketch, "E266.bottom", {"start": v(-37.24, -60) * mm, "end": v(3.51, -60) * mm});
            skLineSegment(sketch, "E266.top", {"start": v(-37.24, -434.82) * mm, "end": v(3.51, -434.82) * mm, "construction": true});
            skLineSegment(sketch, "E266.left", {"start": v(-37.24, -60) * mm, "end": v(-37.24, -434.82) * mm});
            skArc(sketch, "E267", {"start": v(3.51, -434.82) * mm, "mid": v(-16.87, -455.2) * mm, "end": v(-37.24, -434.82) * mm});
            skSolve(sketch);
        }
        {
            var Q0;
            Q0=qCreatedBy(makeId("Front.planeOp"),FACE);
            var sketch = newSketch(context, id + "F8", { "sketchPlane" : qUnion([Q0])});
            skPoint(sketch, "E268.0", {"position": v(-31.38, -60) * mm});
            skPoint(sketch, "E268.1", {"position": v(24.5, -60) * mm});
            skLineSegment(sketch, "E268.2", {"start": v(-1468.77, -1939.1) * mm, "end": v(-1141.9, -2265.96) * mm, "construction": true});
            skLineSegment(sketch, "E269.bottom", {"start": v(2.16, -60) * mm, "end": v(24.5, -60) * mm});
            skLineSegment(sketch, "E269.top", {"start": v(2.16, -522.26) * mm, "end": v(24.5, -522.26) * mm, "construction": true});
            skLineSegment(sketch, "E269.left", {"start": v(2.16, -60) * mm, "end": v(2.16, -522.26) * mm});
            skLineSegment(sketch, "E269.right", {"start": v(24.5, -60) * mm, "end": v(24.5, -522.26) * mm});
            skPoint(sketch, "E270.0", {"position": v(2.16, -60) * mm});
            skLineSegment(sketch, "E271.bottom", {"start": v(-31.38, -60) * mm, "end": v(2.16, -60) * mm});
            skLineSegment(sketch, "E271.top", {"start": v(-31.38, -522.26) * mm, "end": v(2.16, -522.26) * mm, "construction": true});
            skLineSegment(sketch, "E271.right", {"start": v(-31.38, -60) * mm, "end": v(-31.38, -522.26) * mm});
            skArc(sketch, "E272", {"start": v(24.5, -522.26) * mm, "mid": v(13.32, -511.1) * mm, "end": v(2.16, -522.26) * mm});
            skArc(sketch, "E273", {"start": v(2.16, -522.26) * mm, "mid": v(-14.6, -505.5) * mm, "end": v(-31.38, -522.26) * mm});
            skSolve(sketch);
        }
        {
            var Q0;
            Q0=qCreatedBy(makeId("Front.planeOp"),FACE);
            var sketch = newSketch(context, id + "F9", { "sketchPlane" : qUnion([Q0])});
            skLineSegment(sketch, "E274.0", {"start": v(-1457.36, -1449.56) * mm, "end": v(-1230.97, -1664.25) * mm});
            skArc(sketch, "E275.0", {"start": v(-1317.04, -1620) * mm, "mid": v(-1404, -1533.04) * mm, "end": v(-1490.96, -1620) * mm, "construction": true});
            skLineSegment(sketch, "E275.1", {"start": v(-1228.16, -1657.83) * mm, "end": v(1816.82, 1957.9) * mm, "construction": true});
            skLineSegment(sketch, "E276.0", {"start": v(-1460.04, -1449.09) * mm, "end": v(1816.78, 1957.86) * mm, "construction": true});
            skPoint(sketch, "E277.0", {"position": v(-1344.16, -1556.9) * mm});
            skLineSegment(sketch, "E278", {"start": v(-1344.16, -1556.9) * mm, "end": v(1908.53, 1873.1) * mm, "construction": true});
            skLineSegment(sketch, "E279", {"start": v(-1457.36, -1449.56) * mm, "end": v(-1455.59, -1447.7) * mm, "construction": true});
            skLineSegment(sketch, "E280", {"start": v(-1455.59, -1447.7) * mm, "end": v(1908.53, 1873.1) * mm, "construction": true});
            skLineSegment(sketch, "E281", {"start": v(-1230.97, -1664.25) * mm, "end": v(-1229.2, -1662.38) * mm, "construction": true});
            skLineSegment(sketch, "E282", {"start": v(-1229.2, -1662.38) * mm, "end": v(1908.56, 1873.13) * mm, "construction": true});
            skLineSegment(sketch, "E283", {"start": v(1908.56, 1873.13) * mm, "end": v(-1344.16, -1556.9) * mm, "construction": true});
            skLineSegment(sketch, "E284.0", {"start": v(-2210, -1620) * mm, "end": v(-1640.07, -1050.07) * mm, "construction": true});
            skLineSegment(sketch, "E285.0", {"start": v(-50, -60) * mm, "end": v(50, -60) * mm, "construction": true});
            skLineSegment(sketch, "E286", {"start": v(-31.44, -60) * mm, "end": v(-1455.59, -1447.7) * mm, "construction": true});
            skLineSegment(sketch, "E287", {"start": v(-1455.59, -1447.7) * mm, "end": v(-885.66, -877.76) * mm, "construction": true});
            skLineSegment(sketch, "E288", {"start": v(30.76, -60) * mm, "end": v(-1229.2, -1662.38) * mm, "construction": true});
            skLineSegment(sketch, "E289", {"start": v(-1229.2, -1662.38) * mm, "end": v(-659.27, -1092.45) * mm, "construction": true});
            skLineSegment(sketch, "E290", {"start": v(-659.27, -1092.45) * mm, "end": v(-879.8, -871.91) * mm, "construction": true});
            skLineSegment(sketch, "E291.0", {"start": v(1249.15, -1531) * mm, "end": v(1561.13, -1535.1) * mm});
            skPoint(sketch, "E292.0", {"position": v(1405.14, -1533.05) * mm});
            skArc(sketch, "E293.0", {"start": v(1490.96, -1620) * mm, "mid": v(1404, -1533.04) * mm, "end": v(1317.04, -1620) * mm, "construction": true});
            skLineSegment(sketch, "E294", {"start": v(1405.14, -1533.05) * mm, "end": v(1467.17, 3193.58) * mm, "construction": true});
            skLineSegment(sketch, "E295", {"start": v(1467.17, 3193.58) * mm, "end": v(1561.16, -1532.52) * mm, "construction": true});
            skLineSegment(sketch, "E296", {"start": v(1561.16, -1532.52) * mm, "end": v(1561.13, -1535.1) * mm, "construction": true});
            skLineSegment(sketch, "E297", {"start": v(1405.14, -1533.05) * mm, "end": v(1467.17, 3193.63) * mm, "construction": true});
            skLineSegment(sketch, "E298", {"start": v(1467.17, 3193.63) * mm, "end": v(1249.19, -1528.43) * mm, "construction": true});
            skLineSegment(sketch, "E299", {"start": v(1249.19, -1528.43) * mm, "end": v(1249.15, -1531) * mm, "construction": true});
            skLineSegment(sketch, "E300", {"start": v(1249.19, -1528.43) * mm, "end": v(679.26, -2098.36) * mm, "construction": true});
            skLineSegment(sketch, "E301", {"start": v(1561.16, -1532.52) * mm, "end": v(991.23, -2102.45) * mm, "construction": true});
            skLineSegment(sketch, "E302", {"start": v(1561.16, -1532.52) * mm, "end": v(-33.4, -60) * mm, "construction": true});
            skLineSegment(sketch, "E303", {"start": v(833.2, -1944.42) * mm, "end": v(991.23, -2102.45) * mm, "construction": true});
            skArc(sketch, "E304.0", {"start": v(-50, -60) * mm, "mid": v(-46.6, -23.25) * mm, "end": v(-36.5, 12.24) * mm, "construction": true});
            skArc(sketch, "E305.0", {"start": v(-36.5, 12.24) * mm, "mid": v(-18.82, 24.99) * mm, "end": v(0, 14) * mm, "construction": true});
            skPoint(sketch, "E306.0", {"position": v(18.82, 24.99) * mm});
            skArc(sketch, "E307.0", {"start": v(50, -60) * mm, "mid": v(46.6, -23.25) * mm, "end": v(36.5, 12.24) * mm, "construction": true});
            skCircle(sketch, "E308.0", {"center": v(0, 0) * mm, "radius": 14 * mm, "construction": true});
            skLineSegment(sketch, "E309", {"start": v(29.48, -60) * mm, "end": v(1249.19, -1528.43) * mm, "construction": true});
            skLineSegment(sketch, "E310", {"start": v(-1344.16, -1556.9) * mm, "end": v(-774.24, -986.98) * mm, "construction": true});
            skLineSegment(sketch, "E311", {"start": v(1.78, -60) * mm, "end": v(-1344.16, -1556.9) * mm, "construction": true});
            skLineSegment(sketch, "E312", {"start": v(1405.14, -1533.05) * mm, "end": v(835.21, -2102.98) * mm, "construction": true});
            skLineSegment(sketch, "E313", {"start": v(1405.14, -1533.05) * mm, "end": v(7.45, -60) * mm, "construction": true});
            skLineSegment(sketch, "E314.bottom", {"start": v(-33.4, -60) * mm, "end": v(7.45, -60) * mm});
            skLineSegment(sketch, "E314.top", {"start": v(-33.4, -283.5) * mm, "end": v(7.45, -283.5) * mm, "construction": true});
            skLineSegment(sketch, "E314.left", {"start": v(-33.4, -60) * mm, "end": v(-33.4, -283.5) * mm});
            skLineSegment(sketch, "E314.right", {"start": v(7.45, -60) * mm, "end": v(7.45, -283.5) * mm});
            skLineSegment(sketch, "E315.bottom", {"start": v(7.45, -60) * mm, "end": v(29.48, -60) * mm});
            skLineSegment(sketch, "E315.top", {"start": v(7.45, -283.5) * mm, "end": v(29.48, -283.5) * mm, "construction": true});
            skLineSegment(sketch, "E315.right", {"start": v(29.48, -60) * mm, "end": v(29.48, -283.5) * mm});
            skArc(sketch, "E316", {"start": v(29.48, -283.5) * mm, "mid": v(18.47, -294.5) * mm, "end": v(7.45, -283.5) * mm});
            skArc(sketch, "E317", {"start": v(7.45, -283.5) * mm, "mid": v(-12.97, -303.92) * mm, "end": v(-33.4, -283.5) * mm});
            skSolve(sketch);
        }
        {
            var Q0;
            Q0=qCreatedBy(makeId("Front.planeOp"),FACE);
            var sketch = newSketch(context, id + "F10", { "sketchPlane" : qUnion([Q0])});
            skLineSegment(sketch, "E318.1", {"start": v(-659.27, -1092.45) * mm, "end": v(-879.8, -871.91) * mm, "construction": true});
            skPoint(sketch, "E318.2", {"position": v(1.78, -60) * mm});
            skLineSegment(sketch, "E319.bottom", {"start": v(-31.44, -60) * mm, "end": v(30.76, -60) * mm});
            skLineSegment(sketch, "E319.left", {"start": v(30.76, -60) * mm, "end": v(30.76, -371.9) * mm});
            skLineSegment(sketch, "E319.right", {"start": v(-31.44, -60) * mm, "end": v(-31.44, -371.9) * mm});
            skPoint(sketch, "E320.0", {"position": v(30.76, -60) * mm});
            skLineSegment(sketch, "E321.bottom", {"start": v(1.78, -60) * mm, "end": v(30.76, -60) * mm});
            skLineSegment(sketch, "E321.top", {"start": v(1.78, -371.9) * mm, "end": v(30.76, -371.9) * mm, "construction": true});
            skLineSegment(sketch, "E321.right", {"start": v(1.78, -60) * mm, "end": v(1.78, -371.9) * mm});
            skPoint(sketch, "E322.0", {"position": v(-31.44, -60) * mm});
            skLineSegment(sketch, "E323", {"start": v(30.76, -371.9) * mm, "end": v(30.76, -371.9) * mm});
            skLineSegment(sketch, "E324", {"start": v(-31.44, -371.9) * mm, "end": v(1.78, -371.9) * mm, "construction": true});
            skArc(sketch, "E325", {"start": v(-31.44, -371.9) * mm, "mid": v(-14.83, -355.28) * mm, "end": v(1.78, -371.9) * mm});
            skArc(sketch, "E326", {"start": v(1.78, -371.9) * mm, "mid": v(16.27, -357.4) * mm, "end": v(30.76, -371.9) * mm});
            skSolve(sketch);
        }
        {
            var Q0;
            Q0=qCreatedBy(makeId("Front.planeOp"),FACE);
            var sketch = newSketch(context, id + "F11", { "sketchPlane" : qUnion([Q0])});
            skLineSegment(sketch, "E327.0", {"start": v(22.59, -1564.41) * mm, "end": v(311.63, -1681.88) * mm, "construction": true});
            skPoint(sketch, "E327.1", {"position": v(0, -1620) * mm});
            skLineSegment(sketch, "E328.0", {"start": v(-765.45, -1564.22) * mm, "end": v(-576.18, -1701.82) * mm, "construction": true});
            skPoint(sketch, "E328.1", {"position": v(-806, -1620) * mm});
            skLineSegment(sketch, "E328.2", {"start": v(-1344.16, -1556.9) * mm, "end": v(-1230.97, -1664.25) * mm, "construction": true});
            skPoint(sketch, "E328.3", {"position": v(-1404, -1620) * mm});
            skLineSegment(sketch, "E328.4", {"start": v(815.85, -1551.74) * mm, "end": v(1047.45, -1585.18) * mm, "construction": true});
            skPoint(sketch, "E328.5", {"position": v(806, -1620) * mm});
            skLineSegment(sketch, "E328.6", {"start": v(1405.14, -1533.05) * mm, "end": v(1561.13, -1535.1) * mm, "construction": true});
            skPoint(sketch, "E328.7", {"position": v(1404, -1620) * mm});
            skLineSegment(sketch, "E329.0", {"start": v(-50, -60) * mm, "end": v(0, -60) * mm, "construction": true});
            skLineSegment(sketch, "E330", {"start": v(-1404, -1620) * mm, "end": v(-1457.36, -1449.56) * mm});
            skLineSegment(sketch, "E331", {"start": v(-954.71, -1426.62) * mm, "end": v(-806, -1620) * mm});
            skLineSegment(sketch, "E332", {"start": v(0, -1620) * mm, "end": v(-266.45, -1446.95) * mm});
            skLineSegment(sketch, "E333", {"start": v(806, -1620) * mm, "end": v(584.25, -1518.3) * mm});
            skLineSegment(sketch, "E334", {"start": v(1249.15, -1531) * mm, "end": v(1404, -1620) * mm});
            skPoint(sketch, "E335.0", {"position": v(-261.02, -1433.57) * mm});
            skLineSegment(sketch, "E336", {"start": v(-266.45, -1446.95) * mm, "end": v(-261.02, -1433.57) * mm});
            skArc(sketch, "E337", {"start": v(22.59, -1564.41) * mm, "mid": v(-120.73, -1502.27) * mm, "end": v(-261.02, -1433.57) * mm});
            skLineSegment(sketch, "E338", {"start": v(22.59, -1564.41) * mm, "end": v(0, -1620) * mm});
            skPoint(sketch, "E339.0", {"position": v(1249.19, -1528.43) * mm});
            skPoint(sketch, "E340.0", {"position": v(-1455.59, -1447.7) * mm});
            skArc(sketch, "E341", {"start": v(-1344.16, -1556.9) * mm, "mid": v(-1400.33, -1502.76) * mm, "end": v(-1455.59, -1447.7) * mm});
            skLineSegment(sketch, "E342", {"start": v(-1455.59, -1447.7) * mm, "end": v(-1457.36, -1449.56) * mm});
            skLineSegment(sketch, "E343", {"start": v(-1404, -1620) * mm, "end": v(-1344.16, -1556.9) * mm});
            skLineSegment(sketch, "E344", {"start": v(1249.15, -1531) * mm, "end": v(1249.19, -1528.43) * mm});
            skArc(sketch, "E345", {"start": v(1405.14, -1533.05) * mm, "mid": v(1327.15, -1531.38) * mm, "end": v(1249.19, -1528.43) * mm});
            skLineSegment(sketch, "E346", {"start": v(1405.14, -1533.05) * mm, "end": v(1404, -1620) * mm});
            skPoint(sketch, "E347.0", {"position": v(585.28, -1511.23) * mm});
            skPoint(sketch, "E348.0", {"position": v(-950.5, -1420.84) * mm});
            skLineSegment(sketch, "E349", {"start": v(-954.71, -1426.62) * mm, "end": v(-950.5, -1420.84) * mm});
            skArc(sketch, "E350", {"start": v(815.85, -1551.74) * mm, "mid": v(700.26, -1533.25) * mm, "end": v(585.28, -1511.23) * mm});
            skLineSegment(sketch, "E351", {"start": v(585.28, -1511.23) * mm, "end": v(584.25, -1518.3) * mm});
            skLineSegment(sketch, "E352", {"start": v(815.85, -1551.74) * mm, "end": v(806, -1620) * mm});
            skArc(sketch, "E353", {"start": v(-765.45, -1564.22) * mm, "mid": v(-859.07, -1493.94) * mm, "end": v(-950.5, -1420.84) * mm});
            skLineSegment(sketch, "E354", {"start": v(-806, -1620) * mm, "end": v(-765.45, -1564.22) * mm});
            skLineSegment(sketch, "E355.0", {"start": v(-2210, -1620) * mm, "end": v(-1640.07, -1050.07) * mm, "construction": true});
            skLineSegment(sketch, "E356", {"start": v(50, -60) * mm, "end": v(569.93, 509.93) * mm});
            skLineSegment(sketch, "E357", {"start": v(0, -60) * mm, "end": v(569.93, 509.93) * mm});
            skLineSegment(sketch, "E358", {"start": v(0, -60) * mm, "end": v(50, -60) * mm});
            skSolve(sketch);
        }
        {
            var Q0;
            Q0 = qSketchRegion(id + "F11", true);
            extrude(context, id + "F12", {"entities" : qUnion([Q0]), "endBound" : BoundingType.SYMMETRIC, "depth" : 25 * mm});
        }
        {
            var Q0;
            Q0=makeQuery(id+"F0.imprint","IMPRINT",FACE,{"disambiguationData":[TD([[makeQuery(id+"F0.imprint","IMPRINT",EDGE,{"derivedFrom":sQuery(id+"F0.wireOp",EDGE,"E4")}),-1.0]])]});
            extrude(context, id + "F13", {"entities" : qUnion([Q0]), "endBound" : BoundingType.SYMMETRIC, "depth" : 100 * mm});
        }
        {
            var Q0;
            Q0=makeQuery(id+"F0.imprint","IMPRINT",FACE,{"disambiguationData":[TD([[makeQuery(id+"F0.imprint","IMPRINT",EDGE,{"derivedFrom":sQuery(id+"F0.wireOp",EDGE,"E0")}),1.0]])]});
            extrude(context, id + "F14", {"entities" : qUnion([Q0]), "endBound" : BoundingType.SYMMETRIC, "depth" : 100 * mm});
        }
        {
            var Q0;
            Q0=makeQuery(id+"F1.imprint","IMPRINT",FACE,{"disambiguationData":[TD([[makeQuery(id+"F1.imprint","IMPRINT",EDGE,{"derivedFrom":sQuery(id+"F1.wireOp",EDGE,"E84")}),-1.0]])]});
            extrude(context, id + "F15", {"entities" : qUnion([Q0]), "depth" : 10 * mm});
        }
        {
            var Q0;
            Q0 = qSketchRegion(id + "F2", true);
            var Q1;
            Q1 = qSketchRegion(id + "F3", true);
            var Q2;
            Q2 = qSketchRegion(id + "F4", true);
            extrude(context, id + "F16", {"entities" : qUnion([Q0, Q1, Q2]), "endBound" : BoundingType.SYMMETRIC, "depth" : 100 * mm});
        }
        {
            var Q0;
            Q0 = qSketchRegion(id + "F6", true);
            extrude(context, id + "F17", {"entities" : qUnion([Q0]), "endBound" : BoundingType.SYMMETRIC, "depth" : 10 * mm});
        }
        {
            var Q0;
            Q0 = qSketchRegion(id + "F7", true);
            extrude(context, id + "F18", {"entities" : qUnion([Q0]), "depth" : 15 * mm, "hasSecondDirection" : true, "secondDirectionOppositeDirection" : false, "secondDirectionDepth" : 5 * mm});
        }
        {
            var Q0;
            Q0 = qSketchRegion(id + "F8", true);
            extrude(context, id + "F19", {"entities" : qUnion([Q0]), "oppositeDirection" : true, "depth" : 15 * mm, "hasSecondDirection" : true, "secondDirectionOppositeDirection" : true, "secondDirectionDepth" : 5 * mm});
        }
        {
            var Q0;
            Q0 = qSketchRegion(id + "F9", true);
            extrude(context, id + "F20", {"entities" : qUnion([Q0]), "depth" : 25 * mm, "hasSecondDirection" : true, "secondDirectionOppositeDirection" : false, "secondDirectionDepth" : 15 * mm});
        }
        {
            var Q0;
            Q0 = qSketchRegion(id + "F10", true);
            extrude(context, id + "F21", {"entities" : qUnion([Q0]), "oppositeDirection" : true, "depth" : 25 * mm, "hasSecondDirection" : true, "secondDirectionOppositeDirection" : true, "secondDirectionDepth" : 15 * mm});
        }
    });
